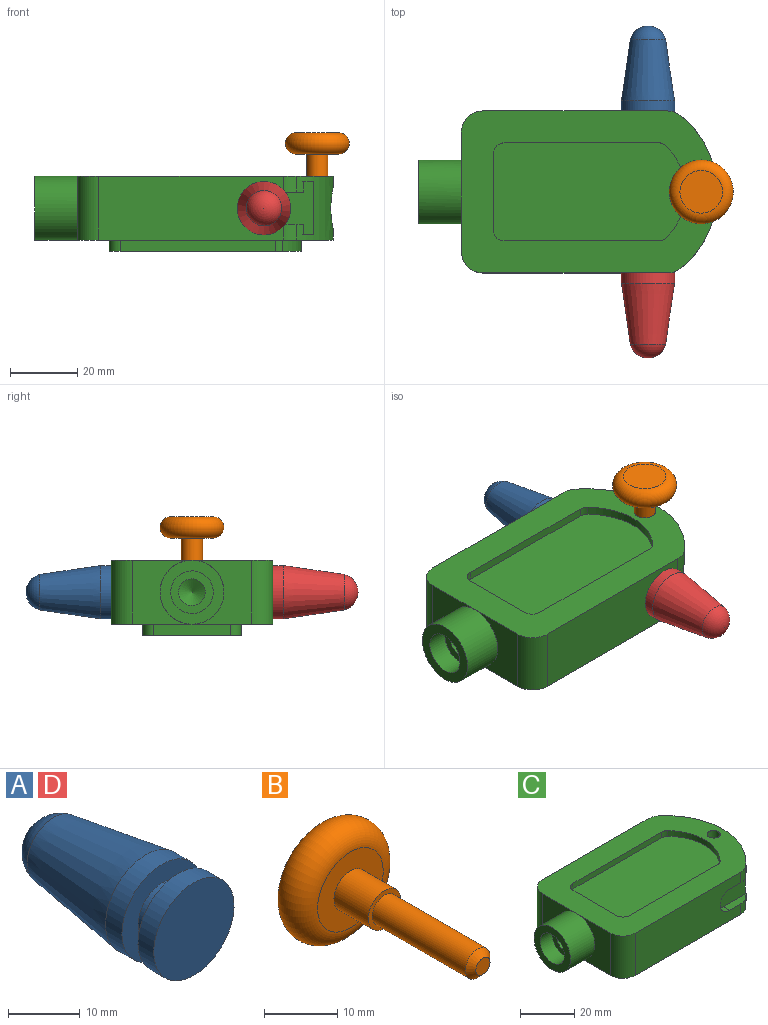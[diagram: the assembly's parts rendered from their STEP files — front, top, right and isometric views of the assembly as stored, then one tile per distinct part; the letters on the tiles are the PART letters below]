
ASSEMBLY  parts=4 mates=7
PART A: 8 faces, bbox 15.9x31.8x15.9 mm
  f0: plane 15.88x15.88mm, normal (0,-1,0), area 197.9mm2, adj f7
  f1: sphere r=5.46mm, area 138.3mm2, adj f2
  f2: cone r=7.94mm half-angle=8.3deg, axis (0,-1,0), area 763mm2, adj f1,f3
  f3: cylinder r=7.94mm len=15.88mm, axis (0,1,0), area 160.9mm2, adj f2,f4
  f4: plane 15.88x15.88mm, normal (0,-1,0), area 127.4mm2, adj f3,f5
  f5: cylinder r=4.74mm len=9.47mm, axis (0,1,0), area 94.5mm2, adj f4,f6
  f6: plane 15.88x15.88mm, normal (0,1,0), area 127.4mm2, adj f5,f7
  f7: cylinder r=7.94mm len=15.88mm, axis (0,1,0), area 155.8mm2, adj f0,f6
PART B: 8 faces, bbox 20.6x32x20.6 mm
  f0: plane 12.7x12.7mm, normal (0,-1,0), area 95mm2, adj f2,f6
  f1: plane 12.7x12.7mm, normal (0,1,0), area 126.7mm2, adj f6
  f2: cylinder r=3.17mm len=6.6mm, axis (0,1,0), area 131.7mm2, adj f0,f3
  f3: plane 6.35x6.35mm, normal (0,-1,0), area 13.9mm2, adj f2,f4
  f4: cylinder r=2.38mm len=18.03mm, axis (0,1,0), area 269.8mm2, adj f3,f7
  f5: plane 2.73x2.73mm, normal (0,-1,0), area 5.9mm2, adj f7
  f6: torus R=6.35mm, axis (0,-1,0), area 524.6mm2, adj f0,f1
  f7: cone r=1.37mm half-angle=45deg, axis (0,1,0), area 16.9mm2, adj f4,f5
PART C: 62 faces, bbox 88.9x48.3x22.4 mm
  f0: plane 54.99x19.05mm, normal (0,1,0), area 956.7mm2, adj f1,f7,f8,f12,f15,f55,f56,f57
  f1: cylinder r=6.35mm len=4.75mm, axis (0,0,-1), area 20.5mm2, adj f0,f2,f8,f56
  f2: cylinder r=29.18mm len=45.45mm, axis (0,0,-1), area 677mm2, adj f1,f3,f7,f8,f14,f15,f44,f46
  f3: cylinder r=6.35mm len=4.75mm, axis (0,0,-1), area 20.5mm2, adj f2,f7,f11,f47
  f4: cylinder r=2.39mm len=4.78mm, axis (0,0,1), area 51.1mm2, adj f8,f44
  f5: cylinder r=2.39mm len=4.78mm, axis (0,0,1), area 51.1mm2, adj f7,f44
  f6: plane 57.15x29.21mm, normal (0,0,-1), area 1108.6mm2, adj f18,f19,f20,f21,f22,f23,f24,f25
  f7: plane 76.2x48.26mm, normal (0,0,1), area 1851.8mm2, adj f0,f2,f3,f5,f9,f10,f11,f12
  f8: plane 76.2x48.26mm, normal (0,0,-1), area 1851.8mm2, adj f0,f1,f2,f4,f9,f10,f11,f12
  f9: plane 19.05x17.78mm, normal (-1,0,0), area 196.2mm2, adj f7,f8,f13,f16
  f10: plane 19.05x17.78mm, normal (-1,0,0), area 196.2mm2, adj f7,f8,f12,f16
  f11: plane 54.99x19.05mm, normal (0,-1,0), area 956.7mm2, adj f3,f7,f8,f13,f14,f47,f48,f49
  f12: cylinder r=6.35mm len=19.05mm, axis (0,0,1), area 190mm2, adj f0,f7,f8,f10
  f13: cylinder r=6.35mm len=19.05mm, axis (0,0,-1), area 190mm2, adj f7,f8,f9,f11
  f14: cylinder r=6.35mm len=4.75mm, axis (0,0,-1), area 20.5mm2, adj f2,f8,f11,f48
  f15: cylinder r=6.35mm len=4.75mm, axis (0,0,-1), area 20.5mm2, adj f0,f2,f7,f55
  f16: cylinder r=9.53mm len=19.05mm, axis (1,0,0), area 760.1mm2, adj f9,f10,f17
  f17: plane 19.05x19.05mm, normal (-1,0,0), area 158.3mm2, adj f16,f28
  f18: plane 46.19x3.3mm, normal (0,1,0), area 152.5mm2, adj f6,f8,f22,f25
  f19: cylinder r=19.66mm len=27.26mm, axis (0,0,1), area 99.5mm2, adj f6,f8,f22,f23
  f20: plane 46.19x3.3mm, normal (0,-1,0), area 152.5mm2, adj f6,f8,f23,f24
  f21: plane 22.86x3.3mm, normal (-1,0,0), area 75.5mm2, adj f6,f8,f24,f25
  f22: cylinder r=3.17mm len=3.3mm, axis (0,0,1), area 8.4mm2, adj f6,f8,f18,f19
  f23: cylinder r=3.17mm len=3.3mm, axis (0,0,1), area 8.4mm2, adj f6,f8,f19,f20
  f24: cylinder r=3.17mm len=3.3mm, axis (0,0,1), area 16.5mm2, adj f6,f8,f20,f21
  f25: cylinder r=3.17mm len=3.3mm, axis (0,0,1), area 16.5mm2, adj f6,f8,f18,f21
  f26: cylinder r=3.97mm len=19.05mm, axis (-1,0,0), area 475mm2, adj f27,f29
  f27: plane 12.7x12.7mm, normal (-1,0,0), area 77.2mm2, adj f26,f28
  f28: cylinder r=6.35mm len=12.7mm, axis (-1,0,0), area 253.4mm2, adj f17,f27
  f29: cone r=0mm half-angle=59deg, axis (-1,0,0), area 57.7mm2, adj f26
  f30: plane 46.19x2.54mm, normal (0,-1,0), area 117.3mm2, adj f7,f31,f37,f38
  f31: cylinder r=3.17mm len=3.18mm, axis (0,0,1), area 12.7mm2, adj f7,f30,f32,f38
  f32: plane 22.86x2.54mm, normal (1,0,0), area 58.1mm2, adj f7,f31,f33,f38
  f33: cylinder r=3.17mm len=3.18mm, axis (0,0,1), area 12.7mm2, adj f7,f32,f34,f38
  f34: plane 46.19x2.54mm, normal (0,1,0), area 117.3mm2, adj f7,f33,f35,f38
  f35: cylinder r=3.17mm len=2.54mm, axis (0,0,1), area 6.5mm2, adj f7,f34,f36,f38
  f36: cylinder r=19.66mm len=27.26mm, axis (0,0,1), area 76.5mm2, adj f7,f35,f37,f38
  f37: cylinder r=3.17mm len=2.54mm, axis (0,0,1), area 6.5mm2, adj f7,f30,f36,f38
  f38: plane 57.15x29.21mm, normal (0,0,1), area 1606.2mm2, adj f30,f31,f32,f33,f34,f35,f36,f37
  f39: plane 29.21x5.08mm, normal (0,1,0), area 148.4mm2, adj f6,f40,f42,f43
  f40: cylinder r=6.35mm len=12.7mm, axis (0,0,-1), area 101.3mm2, adj f6,f39,f41,f43
  f41: plane 29.21x5.08mm, normal (0,-1,0), area 148.4mm2, adj f6,f40,f42,f43
  f42: cylinder r=6.35mm len=12.7mm, axis (0,0,-1), area 101.3mm2, adj f6,f39,f41,f43
  f43: plane 41.91x12.7mm, normal (0,0,-1), area 497.6mm2, adj f39,f40,f41,f42
  f44: cylinder r=6.35mm len=12.7mm, axis (1,0,0), area 405.6mm2, adj f2,f4,f5,f45
  f45: cone r=0mm half-angle=59deg, axis (1,0,0), area 147.8mm2, adj f44
  f46: plane 22.59x15.9mm, normal (0,-1,0), area 332.1mm2, adj f2,f50,f51,f53
  f47: plane 11.83x3.25mm, normal (0,0,-1), area 31.9mm2, adj f2,f3,f11,f49,f52
  f48: plane 11.83x3.25mm, normal (0,0,1), area 31.9mm2, adj f2,f11,f14,f49,f52
  f49: cylinder r=4.78mm len=9.55mm, axis (0,-1,0), area 48.8mm2, adj f11,f47,f48,f52
  f50: plane 14.64x3.18mm, normal (0,0,1), area 42.2mm2, adj f2,f46,f52,f53
  f51: plane 14.64x3.18mm, normal (0,0,-1), area 42.2mm2, adj f2,f46,f52,f53
  f52: plane 19.78x15.9mm, normal (0,1,0), area 138.6mm2, adj f2,f47,f48,f49,f50,f51,f53
  f53: cylinder r=7.95mm len=15.9mm, axis (0,1,0), area 79.3mm2, adj f46,f50,f51,f52
  f54: plane 22.59x15.9mm, normal (0,1,0), area 332.1mm2, adj f2,f58,f59,f61
  f55: plane 11.83x3.25mm, normal (0,0,-1), area 31.9mm2, adj f0,f2,f15,f57,f60
  f56: plane 11.83x3.25mm, normal (0,0,1), area 31.9mm2, adj f0,f1,f2,f57,f60
  f57: cylinder r=4.78mm len=9.55mm, axis (0,1,0), area 48.8mm2, adj f0,f55,f56,f60
  f58: plane 14.64x3.18mm, normal (0,0,-1), area 42.2mm2, adj f2,f54,f60,f61
  f59: plane 14.64x3.18mm, normal (0,0,1), area 42.2mm2, adj f2,f54,f60,f61
  f60: plane 19.78x15.9mm, normal (0,-1,0), area 138.6mm2, adj f2,f55,f56,f57,f58,f59,f61
  f61: cylinder r=7.95mm len=15.9mm, axis (0,-1,0), area 79.3mm2, adj f54,f58,f59,f60
PART D: same geometry as A
PLACE A t=(-27.43,13.35,1.84)mm
PLACE B rot(axis=(1,0,0),90deg) t=(-11.55,-4.36,24.31)mm
PLACE C t=(-35.99,-4.36,-7.69)mm
PLACE D rot(axis=(-1,0,0),180deg) t=(-27.43,-22.06,1.84)mm
MATE cylindrical A.f2 <-> C.f57  axis (0,1,0) through (-27.43,14.91,1.84)mm
MATE cylindrical D.f2 <-> C.f49  axis (0,-1,0) through (-27.43,-23.62,1.84)mm
MATE planar B.f2 <-> C.f7  axis (0,0,-1) through (-11.55,-4.36,11.36)mm
MATE planar D.f2 <-> C.f46  axis (0,1,0) through (-27.43,-22.06,1.84)mm
MATE cylindrical B.f4 <-> C.f4  axis (0,0,1) through (-11.55,-4.36,2.34)mm
MATE planar C.f46 <-> C.f46  axis (0,-1,0) through (-23.31,-22.06,1.84)mm
MATE planar A.f2 <-> C.f54  axis (0,-1,0) through (-27.43,13.35,1.84)mm
